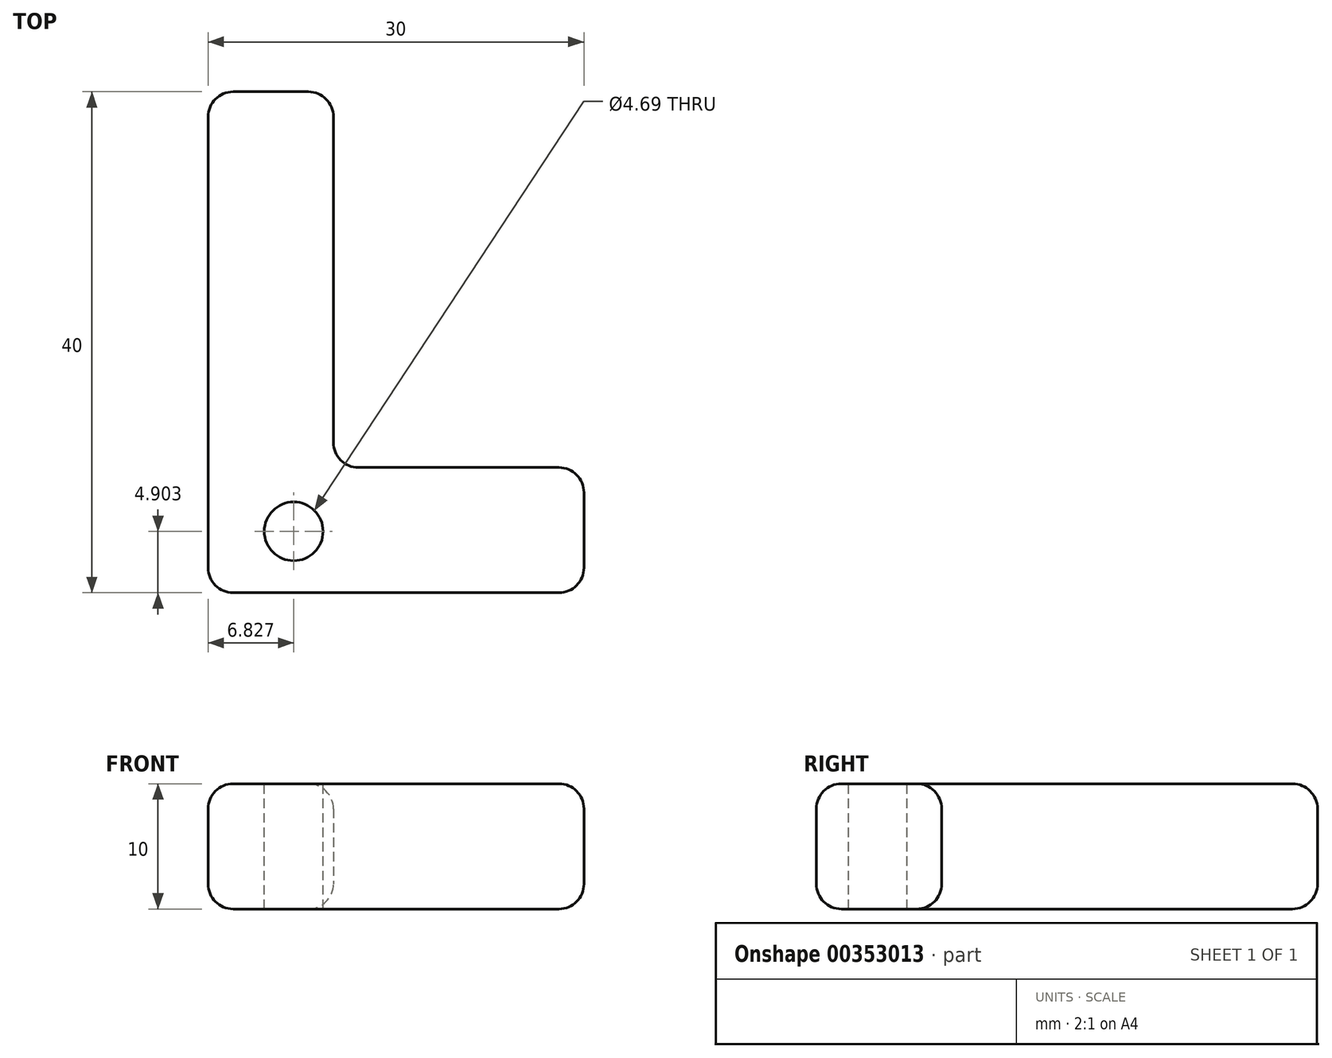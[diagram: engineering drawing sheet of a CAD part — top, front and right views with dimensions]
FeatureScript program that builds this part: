
annotation { "Feature Type Name" : "Feature", "Feature Type Description" : "" }
export const myFeature = defineFeature(function(context is Context, id is Id, definition is map)
    precondition{}
    {
        {
            var Q0;
            Q0=qCreatedBy(makeId("Top.planeOp"),FACE);
            var sketch = newSketch(context, id + "F0", { "sketchPlane" : qUnion([Q0])});
            skLineSegment(sketch, "E0", {"start": v(0, 0) * mm, "end": v(0, 40) * mm});
            skLineSegment(sketch, "E1", {"start": v(0, 40) * mm, "end": v(10, 40) * mm});
            skLineSegment(sketch, "E2", {"start": v(10, 40) * mm, "end": v(10, 10) * mm});
            skLineSegment(sketch, "E3", {"start": v(10, 10) * mm, "end": v(30, 10) * mm});
            skLineSegment(sketch, "E4", {"start": v(30, 10) * mm, "end": v(30, 0) * mm});
            skLineSegment(sketch, "E5", {"start": v(30, 0) * mm, "end": v(0, 0) * mm});
            skSolve(sketch);
        }
        {
            var Q0;
            Q0 = qSketchRegion(id + "F0", true);
            extrude(context, id + "F1", {"entities" : qUnion([Q0]), "depth" : 10 * mm});
        }
        {
            var Q0;
            Q0=makeQuery(id+"F1.opExtrude","CAP_FACE",FACE,{"disambiguationData":[OSD([sQuery(id+"F0.wireOp",EDGE,"E0"),sQuery(id+"F0.wireOp",EDGE,"E1"),sQuery(id+"F0.wireOp",EDGE,"E2"),sQuery(id+"F0.wireOp",EDGE,"E3"),sQuery(id+"F0.wireOp",EDGE,"E4"),sQuery(id+"F0.wireOp",EDGE,"E5")])],"isStart":false});
            var Q1;
            Q1=makeQuery(id+"F1.opExtrude","CAP_FACE",FACE,{"disambiguationData":[OSD([sQuery(id+"F0.wireOp",EDGE,"E0"),sQuery(id+"F0.wireOp",EDGE,"E1"),sQuery(id+"F0.wireOp",EDGE,"E2"),sQuery(id+"F0.wireOp",EDGE,"E3"),sQuery(id+"F0.wireOp",EDGE,"E4"),sQuery(id+"F0.wireOp",EDGE,"E5")])],"isStart":true});
            var Q2;
            Q2=makeQuery(id+"F1.opExtrude","SWEPT_FACE",FACE,{"disambiguationData":[OSD([sQuery(id+"F0.wireOp",EDGE,"E1")])]});
            var Q3;
            Q3=makeQuery(id+"F1.opExtrude","SWEPT_FACE",FACE,{"disambiguationData":[OSD([sQuery(id+"F0.wireOp",EDGE,"E2")])]});
            var Q4;
            Q4=makeQuery(id+"F1.opExtrude","SWEPT_FACE",FACE,{"disambiguationData":[OSD([sQuery(id+"F0.wireOp",EDGE,"E3")])]});
            var Q5;
            Q5=makeQuery(id+"F1.opExtrude","SWEPT_FACE",FACE,{"disambiguationData":[OSD([sQuery(id+"F0.wireOp",EDGE,"E5")])]});
            fillet(context, id + "F2", {"entities" : qUnion([Q0, Q1, Q2, Q3, Q4, Q5]), "radius" : 2 * mm, "tangentPropagation" : true, "allowEdgeOverflow" : false});
        }
        {
            var Q0;
            Q0=makeQuery(id+"F1.opExtrude","CAP_FACE",FACE,{"disambiguationData":[OSD([sQuery(id+"F0.wireOp",EDGE,"E0"),sQuery(id+"F0.wireOp",EDGE,"E1"),sQuery(id+"F0.wireOp",EDGE,"E2"),sQuery(id+"F0.wireOp",EDGE,"E3"),sQuery(id+"F0.wireOp",EDGE,"E4"),sQuery(id+"F0.wireOp",EDGE,"E5")])],"isStart":false});
            var sketch = newSketch(context, id + "F3", { "sketchPlane" : qUnion([Q0])});
            skCircle(sketch, "E6", {"center": v(6.83, 4.9) * mm, "radius": 2.35 * mm});
            skSolve(sketch);
        }
        {
            var Q0;
            Q0 = qSketchRegion(id + "F3", true);
            extrude(context, id + "F4", {"entities" : qUnion([Q0]), "operationType" : NewBodyOperationType.REMOVE, "oppositeDirection" : true, "depth" : 25 * mm});
        }
    });
